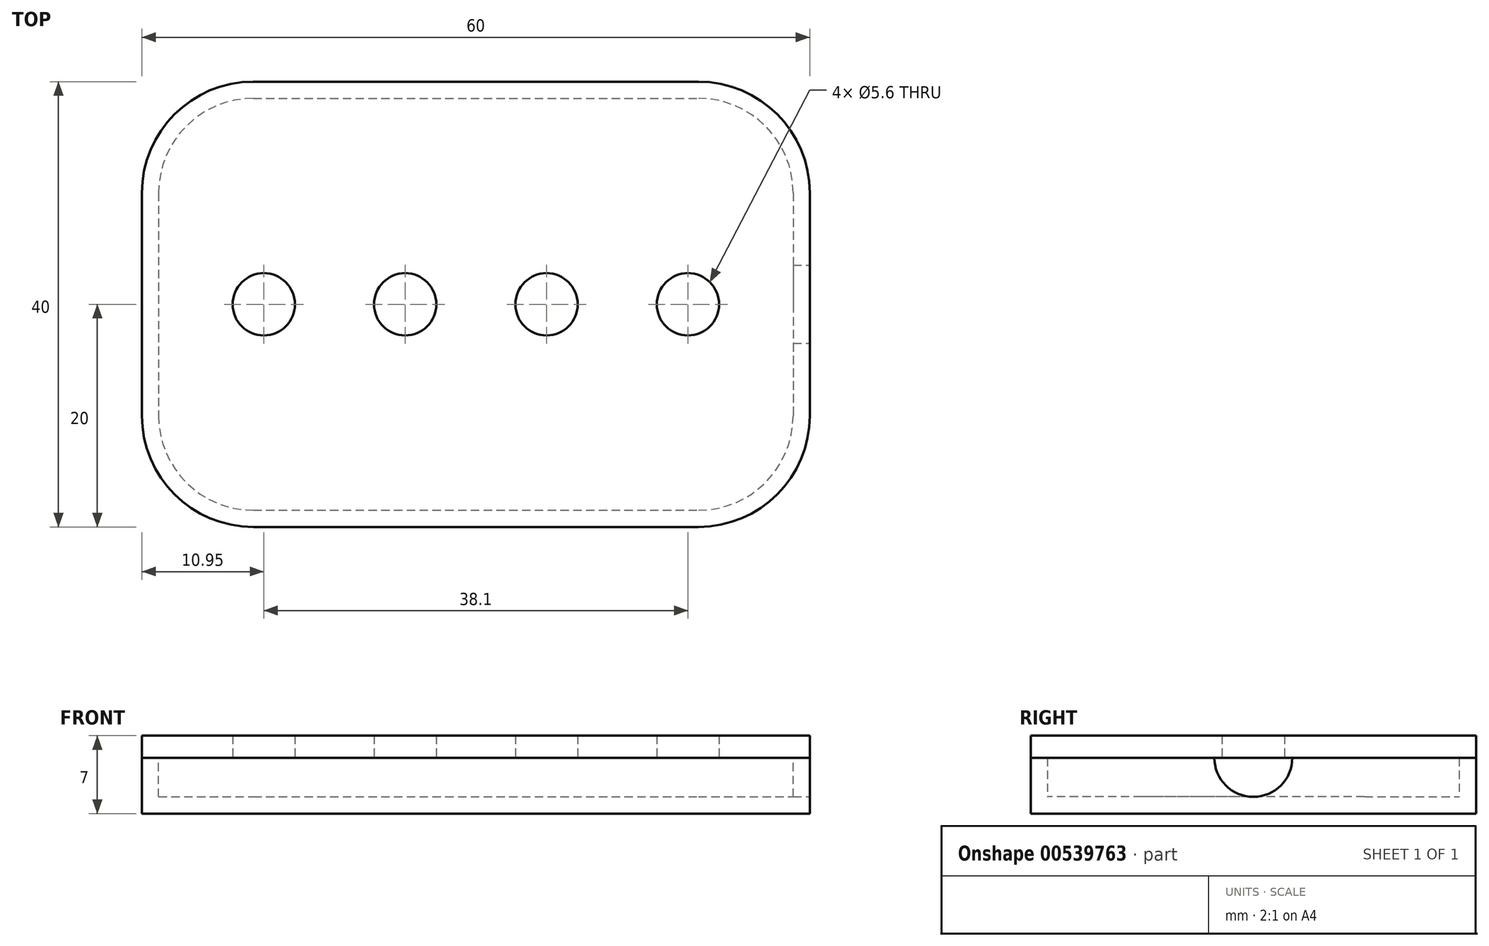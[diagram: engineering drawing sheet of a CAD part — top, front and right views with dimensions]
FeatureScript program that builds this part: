
annotation { "Feature Type Name" : "Feature", "Feature Type Description" : "" }
export const myFeature = defineFeature(function(context is Context, id is Id, definition is map)
    precondition{}
    {
        {
            var Q0;
            Q0=qCreatedBy(makeId("Top.planeOp"),FACE);
            var sketch = newSketch(context, id + "F0", { "sketchPlane" : qUnion([Q0])});
            skLineSegment(sketch, "E0.bottom", {"start": v(-30, 20) * mm, "end": v(30, 20) * mm});
            skLineSegment(sketch, "E0.top", {"start": v(-30, -20) * mm, "end": v(30, -20) * mm});
            skLineSegment(sketch, "E0.left", {"start": v(-30, 20) * mm, "end": v(-30, -20) * mm});
            skLineSegment(sketch, "E0.right", {"start": v(30, 20) * mm, "end": v(30, -20) * mm});
            skPoint(sketch, "E0.middle", {"position": v(0, 0) * mm});
            skCircle(sketch, "E1", {"center": v(-19.05, 0) * mm, "radius": 2.8 * mm});
            skPoint(sketch, "E1.centerSnap0", {"position": v(-30, 0) * mm});
            skCircle(sketch, "E2", {"center": v(-6.35, 0) * mm, "radius": 2.8 * mm});
            skCircle(sketch, "E3", {"center": v(6.35, 0) * mm, "radius": 2.8 * mm});
            skCircle(sketch, "E4", {"center": v(19.05, 0) * mm, "radius": 2.8 * mm});
            skSolve(sketch);
        }
        {
            var Q0;
            Q0 = qSketchRegion(id + "F0", true);
            extrude(context, id + "F1", {"entities" : qUnion([Q0]), "depth" : 2 * mm, "offsetDistance" : 25 * mm});
        }
        {
            var Q0;
            Q0=makeQuery(id+"F1.opExtrude","SWEPT_EDGE",EDGE,{"disambiguationData":[OSD([sQuery(id+"F0.wireOp",EDGE,"E0.bottom"),sQuery(id+"F0.wireOp",EDGE,"E0.left")])]});
            fillet(context, id + "F2", {"entities" : qUnion([Q0]), "radius" : 10 * mm, "tangentPropagation" : true, "allowEdgeOverflow" : false});
        }
        {
            var Q0;
            Q0=makeQuery(id+"F1.opExtrude","SWEPT_EDGE",EDGE,{"disambiguationData":[OSD([sQuery(id+"F0.wireOp",EDGE,"E0.top"),sQuery(id+"F0.wireOp",EDGE,"E0.left")])]});
            fillet(context, id + "F3", {"entities" : qUnion([Q0]), "radius" : 10 * mm, "tangentPropagation" : true, "allowEdgeOverflow" : false});
        }
        {
            var Q0;
            Q0=makeQuery(id+"F1.opExtrude","SWEPT_EDGE",EDGE,{"disambiguationData":[OSD([sQuery(id+"F0.wireOp",EDGE,"E0.top"),sQuery(id+"F0.wireOp",EDGE,"E0.right")])]});
            fillet(context, id + "F4", {"entities" : qUnion([Q0]), "radius" : 10 * mm, "tangentPropagation" : true, "allowEdgeOverflow" : false});
        }
        {
            var Q0;
            Q0=makeQuery(id+"F1.opExtrude","SWEPT_EDGE",EDGE,{"disambiguationData":[OSD([sQuery(id+"F0.wireOp",EDGE,"E0.bottom"),sQuery(id+"F0.wireOp",EDGE,"E0.right")])]});
            fillet(context, id + "F5", {"entities" : qUnion([Q0]), "radius" : 10 * mm, "tangentPropagation" : true, "allowEdgeOverflow" : false});
        }
        {
            var Q0;
            Q0=qCreatedBy(makeId("Top.planeOp"),FACE);
            var sketch = newSketch(context, id + "F6", { "sketchPlane" : qUnion([Q0])});
            skLineSegment(sketch, "E5.bottom", {"start": v(-30, 20) * mm, "end": v(30, 20) * mm});
            skLineSegment(sketch, "E5.top", {"start": v(-30, -20) * mm, "end": v(30, -20) * mm});
            skLineSegment(sketch, "E5.left", {"start": v(-30, 20) * mm, "end": v(-30, -20) * mm});
            skLineSegment(sketch, "E5.right", {"start": v(30, 20) * mm, "end": v(30, -20) * mm});
            skPoint(sketch, "E5.middle", {"position": v(0, 0) * mm});
            skPoint(sketch, "E6.centerSnap0", {"position": v(-30, 0) * mm});
            skSolve(sketch);
        }
        {
            var Q0;
            Q0 = qSketchRegion(id + "F6", true);
            extrude(context, id + "F7", {"entities" : qUnion([Q0]), "oppositeDirection" : true, "depth" : 5 * mm, "offsetDistance" : 25 * mm});
        }
        {
            var Q0;
            Q0=makeQuery(id+"F7.opExtrude","SWEPT_EDGE",EDGE,{"disambiguationData":[OSD([sQuery(id+"F6.wireOp",EDGE,"E5.top"),sQuery(id+"F6.wireOp",EDGE,"E5.left")])]});
            var Q1;
            Q1=makeQuery(id+"F7.opExtrude","SWEPT_EDGE",EDGE,{"disambiguationData":[OSD([sQuery(id+"F6.wireOp",EDGE,"E5.top"),sQuery(id+"F6.wireOp",EDGE,"E5.right")])]});
            var Q2;
            Q2=makeQuery(id+"F7.opExtrude","SWEPT_EDGE",EDGE,{"disambiguationData":[OSD([sQuery(id+"F6.wireOp",EDGE,"E5.bottom"),sQuery(id+"F6.wireOp",EDGE,"E5.right")])]});
            var Q3;
            Q3=makeQuery(id+"F7.opExtrude","SWEPT_EDGE",EDGE,{"disambiguationData":[OSD([sQuery(id+"F6.wireOp",EDGE,"E5.bottom"),sQuery(id+"F6.wireOp",EDGE,"E5.left")])]});
            fillet(context, id + "F8", {"entities" : qUnion([Q0, Q1, Q2, Q3]), "radius" : 10 * mm, "tangentPropagation" : true, "allowEdgeOverflow" : false});
        }
        {
            var Q0;
            Q0=makeQuery(id+"F7.opExtrude","CAP_FACE",FACE,{"disambiguationData":[OSD([sQuery(id+"F6.wireOp",EDGE,"E5.bottom"),sQuery(id+"F6.wireOp",EDGE,"E5.top"),sQuery(id+"F6.wireOp",EDGE,"E5.left"),sQuery(id+"F6.wireOp",EDGE,"E5.right")])],"isStart":true});
            shell(context, id + "F9", {"entities" : qUnion([Q0]), "thickness" : 1.5 * mm});
        }
        {
            var Q0;
            Q0=makeQuery(id+"F7.opExtrude","SWEPT_FACE",FACE,{"disambiguationData":[OSD([sQuery(id+"F6.wireOp",EDGE,"E5.right")])]});
            var sketch = newSketch(context, id + "F10", { "sketchPlane" : qUnion([Q0])});
            skPoint(sketch, "E7", {"position": v(0, 0) * mm});
            skSolve(sketch);
        }
        {
            var Q0;
            Q0=sQuery(id+"F10.wireOp",VERTEX,"E7");
            var Q1;
            Q1=makeQuery(id+"F7.opExtrude","SWEPT_BODY",BODY,{"disambiguationData":[OSD([sQuery(id+"F6.wireOp",EDGE,"E5.bottom"),sQuery(id+"F6.wireOp",EDGE,"E5.top"),sQuery(id+"F6.wireOp",EDGE,"E5.left"),sQuery(id+"F6.wireOp",EDGE,"E5.right")])]});
            hole(context, id + "F11", {"style" : HoleStyle.SIMPLE, "endStyle" : HoleEndStyle.BLIND, "holeDiameter" : 7 * mm, "majorDiameter" : 5 * mm, "holeDepth" : 16.5 * mm, "isTappedThrough" : true, "tappedDepth" : 12 * mm, "tapClearance" : 3, "locations" : qUnion([Q0]), "scope" : qUnion([Q1])});
        }
    });
